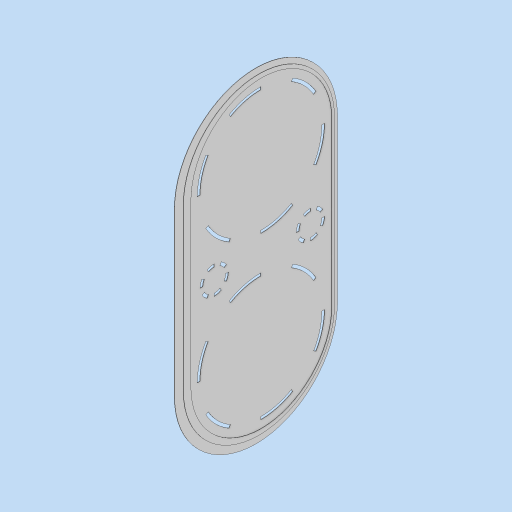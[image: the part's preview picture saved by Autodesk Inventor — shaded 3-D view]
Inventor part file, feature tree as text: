
AUTODESK INVENTOR PART (.ipt)
format: ipt  version: 2024 (Build 280153000, 153)  size: 925,184 bytes
history: native  units: mm
features: extrude x4, sketch x2
ambient origin geometry x8: Origin, YZ Plane, XZ Plane, XY Plane, X Axis, Y Axis, Z Axis, Center Point
bodies: Body1 (feature_tree)
feature tree (6):
  sketch  "Sketch1"  dims[d44=0.25mm d45=0.0mm d46=0.5mm d47=0.0mm]
  extrude  "Extrusion21"  Depth=0.25mm TaperAngle=0.0deg
  extrude  "Extrusion22"  Depth=10.0mm
  extrude  "Extrusion23"  Depth=10.0mm
  extrude  "Extrusion24"  Depth=10.0mm
  sketch  "Sketch4"  dims[d48=0.25mm d49=0.0mm d50=90.0mm d51=57.0mm d52=61.0mm d53=2.0mm d54=30.0deg d55=60.0mm d57=360.0deg d59=0.0mm d60=0.0mm d61=20.0mm d62=28.0mm d63=2.0mm d64=30.0deg d65=60.0mm d67=360.0deg d69=20.0mm d71=68.0mm d72=10.0mm d74=10.0mm d6=0.5mm d7=0.872665mm d8=0.5mm d9=0.872665mm]
